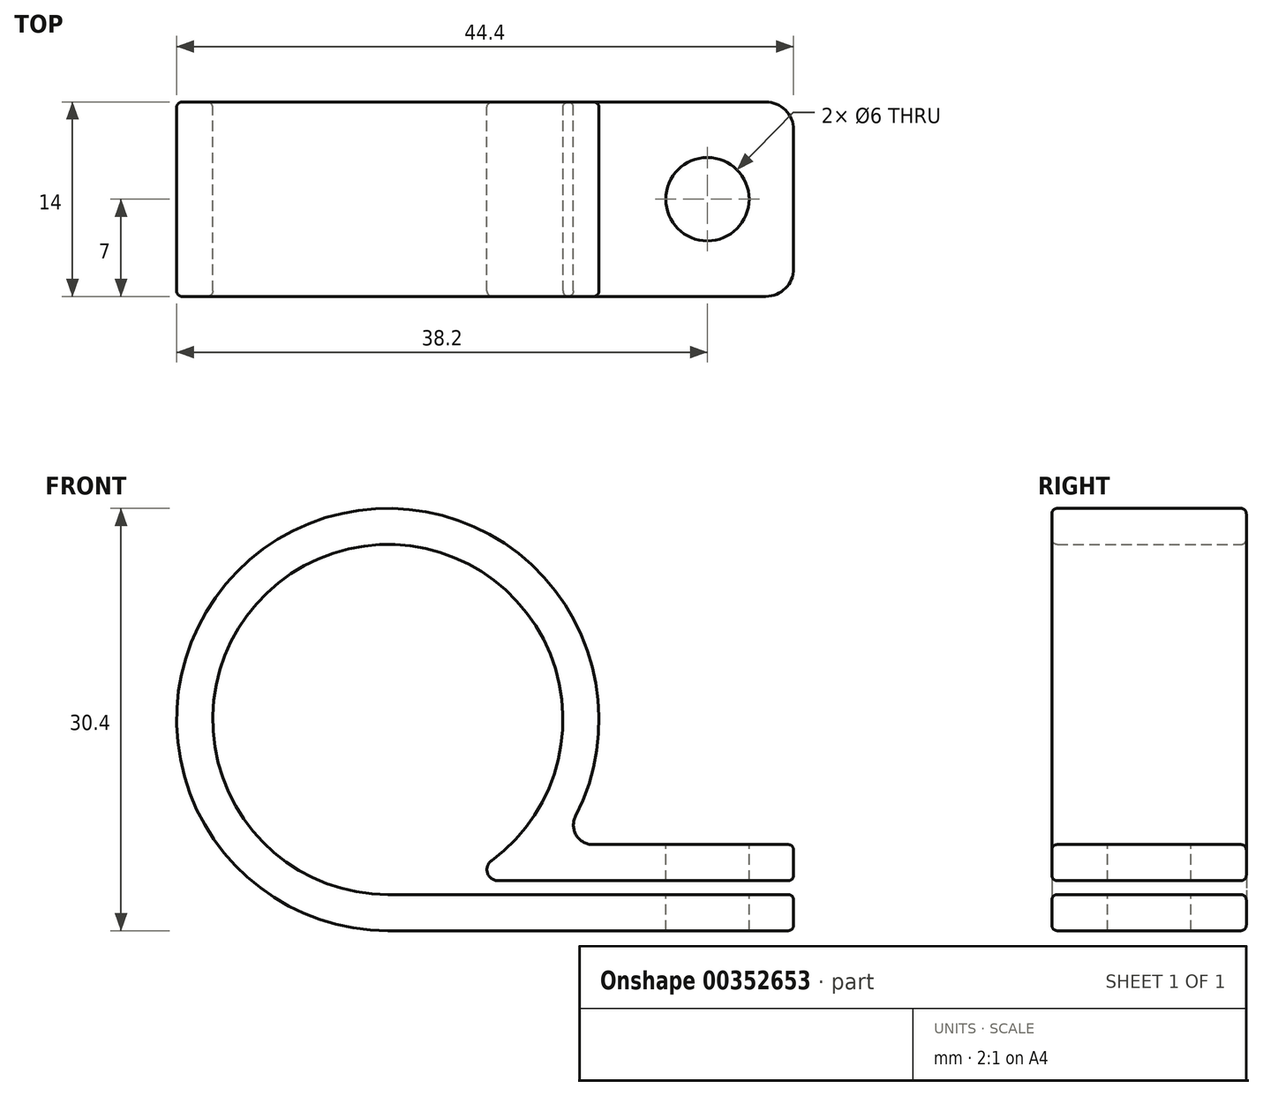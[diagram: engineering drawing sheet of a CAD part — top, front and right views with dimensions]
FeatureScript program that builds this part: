
annotation { "Feature Type Name" : "Feature", "Feature Type Description" : "" }
export const myFeature = defineFeature(function(context is Context, id is Id, definition is map)
    precondition{}
    {
        {
            var Q0;
            Q0=qCreatedBy(makeId("Front.planeOp"),FACE);
            var sketch = newSketch(context, id + "F0", { "sketchPlane" : qUnion([Q0])});
            skCircle(sketch, "E0", {"center": v(0, 0) * mm, "radius": 12.6 * mm});
            skArc(sketch, "E1", {"start": v(12.25, -9) * mm, "mid": v(-6.86, 13.56) * mm, "end": v(0, -15.2) * mm});
            skLineSegment(sketch, "E2", {"start": v(0, -15.2) * mm, "end": v(29.2, -15.2) * mm});
            skLineSegment(sketch, "E3", {"start": v(29.2, -15.2) * mm, "end": v(29.2, -9) * mm});
            skLineSegment(sketch, "E4", {"start": v(29.2, -9) * mm, "end": v(12.25, -9) * mm});
            skLineSegment(sketch, "E5", {"start": v(0, -12.6) * mm, "end": v(29.2, -12.6) * mm});
            skPoint(sketch, "E5.endSnap0", {"position": v(29.2, -12.1) * mm});
            skLineSegment(sketch, "E6", {"start": v(29.2, -11.6) * mm, "end": v(4.92, -11.6) * mm});
            skSolve(sketch);
        }
        {
            var Q0;
            Q0=makeQuery(id+"F0.imprint","IMPRINT",FACE,{"disambiguationData":[TD([[makeQuery(id+"F0.imprint","IMPRINT",EDGE,{"derivedFrom":sQuery(id+"F0.wireOp",EDGE,"E1")}),1.0]])]});
            extrude(context, id + "F1", {"entities" : qUnion([Q0]), "endBound" : BoundingType.SYMMETRIC, "depth" : 14 * mm});
        }
        {
            var Q0;
            {var subQ0=sQuery(id+"F0.wireOp",EDGE,"E3");Q0=makeQuery(id+"F1.opExtrude","CAP_EDGE",EDGE,{"disambiguationData":[OSD([subQ0]),TDD([makeQuery(id+"F0.imprint","IMPRINT",EDGE,{"disambiguationData":[TD([[makeQuery(id+"F0.imprint","INTERSECT",VERTEX,{"derivedFrom":[subQ0,sQuery(id+"F0.wireOp",EDGE,"E4")]}),1.0]])],"derivedFrom":subQ0})])],"isStart":false});}
            var Q1;
            {var subQ0=sQuery(id+"F0.wireOp",EDGE,"E3");Q1=makeQuery(id+"F1.opExtrude","CAP_EDGE",EDGE,{"disambiguationData":[OSD([subQ0]),TDD([makeQuery(id+"F0.imprint","IMPRINT",EDGE,{"disambiguationData":[TD([[makeQuery(id+"F0.imprint","INTERSECT",VERTEX,{"derivedFrom":[sQuery(id+"F0.wireOp",EDGE,"E2"),subQ0]}),-1.0]])],"derivedFrom":subQ0})])],"isStart":false});}
            var Q2;
            {var subQ0=sQuery(id+"F0.wireOp",EDGE,"E3");Q2=makeQuery(id+"F1.opExtrude","CAP_EDGE",EDGE,{"disambiguationData":[OSD([subQ0]),TDD([makeQuery(id+"F0.imprint","IMPRINT",EDGE,{"disambiguationData":[TD([[makeQuery(id+"F0.imprint","INTERSECT",VERTEX,{"derivedFrom":[sQuery(id+"F0.wireOp",EDGE,"E2"),subQ0]}),-1.0]])],"derivedFrom":subQ0})])],"isStart":true});}
            var Q3;
            {var subQ0=sQuery(id+"F0.wireOp",EDGE,"E3");Q3=makeQuery(id+"F1.opExtrude","CAP_EDGE",EDGE,{"disambiguationData":[OSD([subQ0]),TDD([makeQuery(id+"F0.imprint","IMPRINT",EDGE,{"disambiguationData":[TD([[makeQuery(id+"F0.imprint","INTERSECT",VERTEX,{"derivedFrom":[subQ0,sQuery(id+"F0.wireOp",EDGE,"E4")]}),1.0]])],"derivedFrom":subQ0})])],"isStart":true});}
            fillet(context, id + "F2", {"entities" : qUnion([Q0, Q1, Q2, Q3]), "radius" : 2 * mm, "tangentPropagation" : true, "allowEdgeOverflow" : false});
        }
        {
            var Q0;
            Q0=makeQuery(id+"F1.opExtrude","SWEPT_EDGE",EDGE,{"disambiguationData":[OSD([sQuery(id+"F0.wireOp",EDGE,"E1"),sQuery(id+"F0.wireOp",EDGE,"E4")])]});
            fillet(context, id + "F3", {"entities" : qUnion([Q0]), "radius" : 1.4 * mm, "tangentPropagation" : true, "allowEdgeOverflow" : false});
        }
        {
            var Q0;
            Q0=makeQuery(id+"F1.opExtrude","SWEPT_EDGE",EDGE,{"disambiguationData":[OSD([sQuery(id+"F0.wireOp",EDGE,"E0"),sQuery(id+"F0.wireOp",EDGE,"E6")])]});
            fillet(context, id + "F4", {"entities" : qUnion([Q0]), "radius" : 0.8 * mm, "tangentPropagation" : true, "allowEdgeOverflow" : false});
        }
        {
            var Q0;
            Q0=makeQuery(id+"F1.opExtrude","SWEPT_FACE",FACE,{"disambiguationData":[OSD([sQuery(id+"F0.wireOp",EDGE,"E4")])]});
            var sketch = newSketch(context, id + "F5", { "sketchPlane" : qUnion([Q0])});
            skCircle(sketch, "E7", {"center": v(23, 0) * mm, "radius": 3 * mm});
            skPoint(sketch, "E7.centerSnap0", {"position": v(29.2, 0) * mm});
            skSolve(sketch);
        }
        {
            var Q0;
            Q0=makeQuery(id+"F5.imprint","IMPRINT",FACE,{"disambiguationData":[TD([[makeQuery(id+"F5.imprint","IMPRINT",EDGE,{"derivedFrom":sQuery(id+"F5.wireOp",EDGE,"E7")}),1.0]])]});
            extrude(context, id + "F6", {"entities" : qUnion([Q0]), "operationType" : NewBodyOperationType.REMOVE, "endBound" : BoundingType.THROUGH_ALL, "oppositeDirection" : true, "depth" : 25 * mm});
        }
        {
            var Q0;
            Q0=makeQuery(id+"F1.opExtrude","CAP_EDGE",EDGE,{"disambiguationData":[OSD([sQuery(id+"F0.wireOp",EDGE,"E1")])],"isStart":false});
            var Q1;
            Q1=makeQuery(id+"F1.opExtrude","CAP_EDGE",EDGE,{"disambiguationData":[OSD([sQuery(id+"F0.wireOp",EDGE,"E0")])],"isStart":false});
            fillet(context, id + "F7", {"entities" : qUnion([Q0, Q1]), "radius" : 0.4 * mm, "tangentPropagation" : true, "allowEdgeOverflow" : false});
        }
    });
